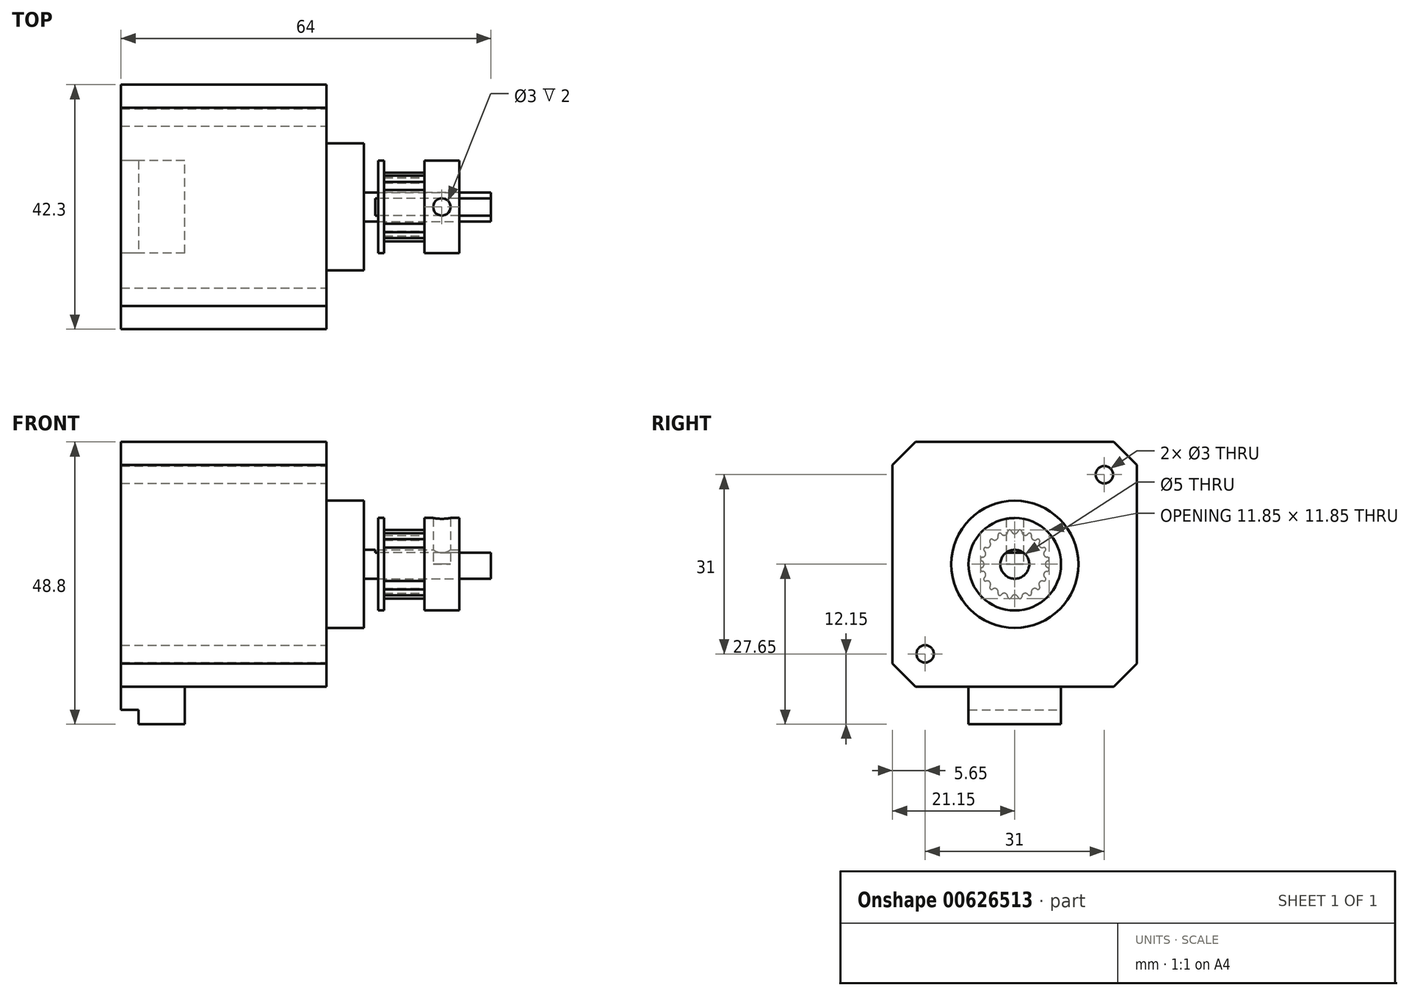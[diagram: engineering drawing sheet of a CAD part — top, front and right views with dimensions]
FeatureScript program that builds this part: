
annotation { "Feature Type Name" : "Feature", "Feature Type Description" : "" }
export const myFeature = defineFeature(function(context is Context, id is Id, definition is map)
    precondition{}
    {
        {
            var Q0;
            Q0=qCreatedBy(makeId("Right.planeOp"),FACE);
            var sketch = newSketch(context, id + "F0", { "sketchPlane" : qUnion([Q0]), "asVersion" : FeatureScriptVersionNumber.V275_SKETCH_PATTERN_LOWER_LIMIT});
            skLineSegment(sketch, "E0", {"start": v(0, 0) * mm, "end": v(-19.15, 19.15) * mm, "construction": true});
            skLineSegment(sketch, "E1", {"start": v(-19.15, 19.15) * mm, "end": v(-17.15, 21.15) * mm});
            skLineSegment(sketch, "E2", {"start": v(-17.15, 21.15) * mm, "end": v(0, 21.15) * mm});
            skCircle(sketch, "E3", {"center": v(-15.5, 15.5) * mm, "radius": 1.5 * mm});
            skLineSegment(sketch, "E4.MirrorCS", {"start": v(-19.15, 19.15) * mm, "end": v(-21.15, 17.15) * mm});
            skLineSegment(sketch, "E5.MirrorCS", {"start": v(-21.15, 17.15) * mm, "end": v(-21.15, 0) * mm});
            skLineSegment(sketch, "E6.MirrorCS", {"start": v(17.15, 21.15) * mm, "end": v(0, 21.15) * mm});
            skCircle(sketch, "E7.MirrorC", {"center": v(15.5, 15.5) * mm, "radius": 1.5 * mm});
            skLineSegment(sketch, "E8.MirrorCS", {"start": v(19.15, 19.15) * mm, "end": v(17.15, 21.15) * mm});
            skLineSegment(sketch, "E9.MirrorCS", {"start": v(19.15, 19.15) * mm, "end": v(21.15, 17.15) * mm});
            skLineSegment(sketch, "E10.MirrorCS", {"start": v(21.15, 17.15) * mm, "end": v(21.15, 0) * mm});
            skLineSegment(sketch, "E11.MirrorCS", {"start": v(-21.15, -17.15) * mm, "end": v(-21.15, 0) * mm});
            skLineSegment(sketch, "E12.MirrorCS", {"start": v(-19.15, -19.15) * mm, "end": v(-21.15, -17.15) * mm});
            skLineSegment(sketch, "E13.MirrorCS", {"start": v(-19.15, -19.15) * mm, "end": v(-17.15, -21.15) * mm});
            skCircle(sketch, "E14.MirrorC", {"center": v(-15.5, -15.5) * mm, "radius": 1.5 * mm});
            skLineSegment(sketch, "E15.MirrorCS", {"start": v(-17.15, -21.15) * mm, "end": v(0, -21.15) * mm});
            skLineSegment(sketch, "E16.MirrorCS", {"start": v(17.15, -21.15) * mm, "end": v(0, -21.15) * mm});
            skLineSegment(sketch, "E17.MirrorCS", {"start": v(19.15, -19.15) * mm, "end": v(17.15, -21.15) * mm});
            skCircle(sketch, "E18.MirrorC", {"center": v(15.5, -15.5) * mm, "radius": 1.5 * mm});
            skLineSegment(sketch, "E19.MirrorCS", {"start": v(19.15, -19.15) * mm, "end": v(21.15, -17.15) * mm});
            skLineSegment(sketch, "E20.MirrorCS", {"start": v(21.15, -17.15) * mm, "end": v(21.15, 0) * mm});
            skCircle(sketch, "E21", {"center": v(0, 0) * mm, "radius": 11 * mm});
            skCircle(sketch, "E22", {"center": v(0, 0) * mm, "radius": 2.5 * mm});
            skLineSegment(sketch, "E23", {"start": v(-1.5, 2) * mm, "end": v(1.5, 2) * mm});
            skSolve(sketch);
        }
        {
            var Q0;
            {var subQ0=sQuery(id+"F0.wireOp",EDGE,"E23");Q0=makeQuery(id+"F0.imprint","IMPRINT",FACE,{"disambiguationData":[TD([[makeQuery(id+"F0.imprint","IMPRINT",EDGE,{"derivedFrom":subQ0}),1.0]])]});}
            var Q1;
            {var subQ0=sQuery(id+"F0.wireOp",EDGE,"E23");Q1=makeQuery(id+"F0.imprint","IMPRINT",FACE,{"disambiguationData":[TD([[makeQuery(id+"F0.imprint","IMPRINT",EDGE,{"derivedFrom":subQ0}),-1.0]])]});}
            var Q2;
            Q2=makeQuery(id+"F0.imprint","IMPRINT",FACE,{"disambiguationData":[TD([[makeQuery(id+"F0.imprint","IMPRINT",EDGE,{"derivedFrom":sQuery(id+"F0.wireOp",EDGE,"E21")}),1.0]])]});
            var Q3;
            Q3=makeQuery(id+"F0.imprint","IMPRINT",FACE,{"disambiguationData":[TD([[makeQuery(id+"F0.imprint","IMPRINT",EDGE,{"derivedFrom":sQuery(id+"F0.wireOp",EDGE,"E7.MirrorC")}),-1.0]])]});
            var Q4;
            Q4=makeQuery(id+"F0.imprint","IMPRINT",FACE,{"disambiguationData":[TD([[makeQuery(id+"F0.imprint","IMPRINT",EDGE,{"derivedFrom":sQuery(id+"F0.wireOp",EDGE,"E18.MirrorC")}),1.0]])]});
            var Q5;
            Q5=makeQuery(id+"F0.imprint","IMPRINT",FACE,{"disambiguationData":[TD([[makeQuery(id+"F0.imprint","IMPRINT",EDGE,{"derivedFrom":sQuery(id+"F0.wireOp",EDGE,"E14.MirrorC")}),-1.0]])]});
            var Q6;
            Q6=makeQuery(id+"F0.imprint","IMPRINT",FACE,{"disambiguationData":[TD([[makeQuery(id+"F0.imprint","IMPRINT",EDGE,{"derivedFrom":sQuery(id+"F0.wireOp",EDGE,"E3")}),1.0]])]});
            var Q7;
            Q7=makeQuery(id+"F0.imprint","IMPRINT",FACE,{"disambiguationData":[TD([[makeQuery(id+"F0.imprint","IMPRINT",EDGE,{"derivedFrom":sQuery(id+"F0.wireOp",EDGE,"E1")}),-1.0]])]});
            extrude(context, id + "F1", {"entities" : qUnion([Q0, Q1, Q2, Q3, Q4, Q5, Q6, Q7]), "oppositeDirection" : true, "depth" : 40 * mm});
        }
        {
            var Q0;
            {var subQ0=sQuery(id+"F0.wireOp",EDGE,"E23");Q0=makeQuery(id+"F0.imprint","IMPRINT",FACE,{"disambiguationData":[TD([[makeQuery(id+"F0.imprint","IMPRINT",EDGE,{"derivedFrom":subQ0}),-1.0]])]});}
            extrude(context, id + "F2", {"entities" : qUnion([Q0]), "operationType" : NewBodyOperationType.ADD, "depth" : 24 * mm});
        }
        {
            var Q0;
            {var subQ0=sQuery(id+"F0.wireOp",EDGE,"E23");Q0=makeQuery(id+"F0.imprint","IMPRINT",FACE,{"disambiguationData":[TD([[makeQuery(id+"F0.imprint","IMPRINT",EDGE,{"derivedFrom":subQ0}),1.0]])]});}
            extrude(context, id + "F3", {"entities" : qUnion([Q0]), "operationType" : NewBodyOperationType.ADD, "depth" : 4 * mm});
        }
        {
            var Q0;
            Q0=makeQuery(id+"F0.imprint","IMPRINT",FACE,{"disambiguationData":[TD([[makeQuery(id+"F0.imprint","IMPRINT",EDGE,{"derivedFrom":sQuery(id+"F0.wireOp",EDGE,"E21")}),1.0]])]});
            extrude(context, id + "F4", {"entities" : qUnion([Q0]), "operationType" : NewBodyOperationType.ADD, "depth" : 2 * mm});
        }
        {
            var Q0;
            Q0=makeQuery(id+"F0.imprint","IMPRINT",FACE,{"disambiguationData":[TD([[makeQuery(id+"F0.imprint","IMPRINT",EDGE,{"derivedFrom":sQuery(id+"F0.wireOp",EDGE,"E3")}),1.0]])]});
            var Q1;
            Q1=makeQuery(id+"F0.imprint","IMPRINT",FACE,{"disambiguationData":[TD([[makeQuery(id+"F0.imprint","IMPRINT",EDGE,{"derivedFrom":sQuery(id+"F0.wireOp",EDGE,"E7.MirrorC")}),-1.0]])]});
            var Q2;
            Q2=makeQuery(id+"F0.imprint","IMPRINT",FACE,{"disambiguationData":[TD([[makeQuery(id+"F0.imprint","IMPRINT",EDGE,{"derivedFrom":sQuery(id+"F0.wireOp",EDGE,"E18.MirrorC")}),1.0]])]});
            var Q3;
            Q3=makeQuery(id+"F0.imprint","IMPRINT",FACE,{"disambiguationData":[TD([[makeQuery(id+"F0.imprint","IMPRINT",EDGE,{"derivedFrom":sQuery(id+"F0.wireOp",EDGE,"E14.MirrorC")}),-1.0]])]});
            extrude(context, id + "F5", {"entities" : qUnion([Q0, Q1, Q2, Q3]), "operationType" : NewBodyOperationType.REMOVE, "oppositeDirection" : true, "depth" : 4.5 * mm});
        }
        {
            var Q0;
            Q0=makeQuery(id+"F1.opExtrude","CAP_FACE",FACE,{"disambiguationData":[OSD([sQuery(id+"F0.wireOp",EDGE,"E1"),sQuery(id+"F0.wireOp",EDGE,"E2"),sQuery(id+"F0.wireOp",EDGE,"E4.MirrorCS"),sQuery(id+"F0.wireOp",EDGE,"E5.MirrorCS"),sQuery(id+"F0.wireOp",EDGE,"E6.MirrorCS"),sQuery(id+"F0.wireOp",EDGE,"E8.MirrorCS"),sQuery(id+"F0.wireOp",EDGE,"E9.MirrorCS"),sQuery(id+"F0.wireOp",EDGE,"E10.MirrorCS"),sQuery(id+"F0.wireOp",EDGE,"E11.MirrorCS"),sQuery(id+"F0.wireOp",EDGE,"E12.MirrorCS"),sQuery(id+"F0.wireOp",EDGE,"E13.MirrorCS"),sQuery(id+"F0.wireOp",EDGE,"E15.MirrorCS"),sQuery(id+"F0.wireOp",EDGE,"E16.MirrorCS"),sQuery(id+"F0.wireOp",EDGE,"E17.MirrorCS"),sQuery(id+"F0.wireOp",EDGE,"E19.MirrorCS"),sQuery(id+"F0.wireOp",EDGE,"E20.MirrorCS")])],"isStart":false});
            var sketch = newSketch(context, id + "F6", { "sketchPlane" : qUnion([Q0]), "asVersion" : FeatureScriptVersionNumber.V275_SKETCH_PATTERN_LOWER_LIMIT});
            skLineSegment(sketch, "E24", {"start": v(-8, -21.15) * mm, "end": v(-8, -27.65) * mm});
            skLineSegment(sketch, "E25.MirrorCS", {"start": v(8, -21.15) * mm, "end": v(8, -27.65) * mm});
            skLineSegment(sketch, "E26", {"start": v(-8, -27.65) * mm, "end": v(8, -27.65) * mm});
            skLineSegment(sketch, "E27", {"start": v(-8, -21.15) * mm, "end": v(8, -21.15) * mm});
            skLineSegment(sketch, "E28", {"start": v(8, -25.15) * mm, "end": v(-8, -25.15) * mm});
            skSolve(sketch);
        }
        {
            var Q0;
            {var subQ0=sQuery(id+"F6.wireOp",EDGE,"E27");Q0=makeQuery(id+"F6.imprint","IMPRINT",FACE,{"disambiguationData":[TD([[makeQuery(id+"F6.imprint","IMPRINT",EDGE,{"derivedFrom":subQ0}),1.0]])]});}
            var Q1;
            {var subQ1=sQuery(id+"F6.wireOp",EDGE,"E26");Q1=makeQuery(id+"F6.imprint","IMPRINT",FACE,{"disambiguationData":[TD([[makeQuery(id+"F6.imprint","IMPRINT",EDGE,{"derivedFrom":subQ1}),1.0]])]});}
            extrude(context, id + "F7", {"entities" : qUnion([Q0, Q1]), "operationType" : NewBodyOperationType.ADD, "oppositeDirection" : true, "depth" : 11 * mm});
        }
        {
            var Q0;
            {var subQ1=sQuery(id+"F6.wireOp",EDGE,"E26");Q0=makeQuery(id+"F6.imprint","IMPRINT",FACE,{"disambiguationData":[TD([[makeQuery(id+"F6.imprint","IMPRINT",EDGE,{"derivedFrom":subQ1}),1.0]])]});}
            extrude(context, id + "F8", {"entities" : qUnion([Q0]), "operationType" : NewBodyOperationType.REMOVE, "oppositeDirection" : true, "depth" : 3 * mm});
        }
        {
            var Q0;
            Q0=qCreatedBy(makeId("Right.planeOp"),FACE);
            cPlane(context, id + "F9", {"entities" : qUnion([Q0]), "cplaneType" : CPlaneType.OFFSET, "offset" : 9 * mm, "width" : 150 * mm, "height" : 150 * mm});
        }
        {
            var Q0;
            Q0=qCreatedBy(id+"F9.planeOp",FACE);
            var sketch = newSketch(context, id + "F10", { "sketchPlane" : qUnion([Q0]), "asVersion" : FeatureScriptVersionNumber.V275_SKETCH_PATTERN_LOWER_LIMIT});
            skCircle(sketch, "E29", {"center": v(0, 0) * mm, "radius": 8 * mm});
            skCircle(sketch, "E30", {"center": v(0, 0) * mm, "radius": 2.5 * mm});
            skSolve(sketch);
        }
        {
            var Q0;
            Q0=makeQuery(id+"F10.imprint","IMPRINT",FACE,{"disambiguationData":[TD([[makeQuery(id+"F10.imprint","IMPRINT",EDGE,{"derivedFrom":sQuery(id+"F10.wireOp",EDGE,"E29")}),1.0]])]});
            extrude(context, id + "F11", {"entities" : qUnion([Q0]), "oppositeDirection" : true, "depth" : 4.5 * mm, "hasSecondDirection" : true, "secondDirectionOppositeDirection" : false, "secondDirectionDepth" : 9.5 * mm});
        }
        {
            var Q0;
            Q0=qCreatedBy(id+"F9.planeOp",FACE);
            var sketch = newSketch(context, id + "F12", { "sketchPlane" : qUnion([Q0]), "asVersion" : FeatureScriptVersionNumber.V275_SKETCH_PATTERN_LOWER_LIMIT});
            skArc(sketch, "E31", {"start": v(-0.57, 5.7) * mm, "mid": v(0, 5.3) * mm, "end": v(0.57, 5.7) * mm});
            skArc(sketch, "E32", {"start": v(0.94, 5.93) * mm, "mid": v(0.71, 5.88) * mm, "end": v(0.57, 5.7) * mm});
            skLineSegment(sketch, "E33", {"start": v(0, 5.9) * mm, "end": v(0, 0) * mm, "construction": true});
            skLineSegment(sketch, "E34", {"start": v(0, 0) * mm, "end": v(0.94, 5.93) * mm, "construction": true});
            skArc(sketch, "E35.MirrorCS", {"start": v(-0.94, 5.93) * mm, "mid": v(-0.71, 5.88) * mm, "end": v(-0.57, 5.7) * mm});
            skArc(sketch, "E36.1.0", {"start": v(2.72, 5.35) * mm, "mid": v(2.5, 5.37) * mm, "end": v(2.3, 5.25) * mm});
            skArc(sketch, "E36.1.1", {"start": v(1.22, 5.6) * mm, "mid": v(1.64, 5.04) * mm, "end": v(2.3, 5.25) * mm});
            skArc(sketch, "E36.1.2", {"start": v(0.94, 5.93) * mm, "mid": v(1.14, 5.81) * mm, "end": v(1.22, 5.6) * mm});
            skArc(sketch, "E36.2.0", {"start": v(4.24, 4.24) * mm, "mid": v(4.03, 4.34) * mm, "end": v(3.81, 4.28) * mm});
            skArc(sketch, "E36.2.1", {"start": v(2.9, 4.95) * mm, "mid": v(3.12, 4.29) * mm, "end": v(3.81, 4.28) * mm});
            skArc(sketch, "E36.2.2", {"start": v(2.72, 5.35) * mm, "mid": v(2.88, 5.18) * mm, "end": v(2.9, 4.95) * mm});
            skArc(sketch, "E36.3.0", {"start": v(5.35, 2.72) * mm, "mid": v(5.18, 2.88) * mm, "end": v(4.95, 2.9) * mm});
            skArc(sketch, "E36.3.1", {"start": v(4.28, 3.81) * mm, "mid": v(4.29, 3.12) * mm, "end": v(4.95, 2.9) * mm});
            skArc(sketch, "E36.3.2", {"start": v(4.24, 4.24) * mm, "mid": v(4.34, 4.03) * mm, "end": v(4.28, 3.81) * mm});
            skArc(sketch, "E36.4.0", {"start": v(5.93, 0.94) * mm, "mid": v(5.81, 1.14) * mm, "end": v(5.6, 1.22) * mm});
            skArc(sketch, "E36.4.1", {"start": v(5.25, 2.3) * mm, "mid": v(5.04, 1.64) * mm, "end": v(5.6, 1.22) * mm});
            skArc(sketch, "E36.4.2", {"start": v(5.35, 2.72) * mm, "mid": v(5.37, 2.5) * mm, "end": v(5.25, 2.3) * mm});
            skArc(sketch, "E36.5.0", {"start": v(5.93, -0.94) * mm, "mid": v(5.88, -0.71) * mm, "end": v(5.7, -0.57) * mm});
            skArc(sketch, "E36.5.1", {"start": v(5.7, 0.57) * mm, "mid": v(5.3, 0) * mm, "end": v(5.7, -0.57) * mm});
            skArc(sketch, "E36.5.2", {"start": v(5.93, 0.94) * mm, "mid": v(5.88, 0.71) * mm, "end": v(5.7, 0.57) * mm});
            skArc(sketch, "E36.6.0", {"start": v(5.35, -2.72) * mm, "mid": v(5.37, -2.5) * mm, "end": v(5.25, -2.3) * mm});
            skArc(sketch, "E36.6.1", {"start": v(5.6, -1.22) * mm, "mid": v(5.04, -1.64) * mm, "end": v(5.25, -2.3) * mm});
            skArc(sketch, "E36.6.2", {"start": v(5.93, -0.94) * mm, "mid": v(5.81, -1.14) * mm, "end": v(5.6, -1.22) * mm});
            skArc(sketch, "E36.7.0", {"start": v(4.24, -4.24) * mm, "mid": v(4.34, -4.03) * mm, "end": v(4.28, -3.81) * mm});
            skArc(sketch, "E36.7.1", {"start": v(4.95, -2.9) * mm, "mid": v(4.29, -3.12) * mm, "end": v(4.28, -3.81) * mm});
            skArc(sketch, "E36.7.2", {"start": v(5.35, -2.72) * mm, "mid": v(5.18, -2.88) * mm, "end": v(4.95, -2.9) * mm});
            skArc(sketch, "E36.8.0", {"start": v(2.72, -5.35) * mm, "mid": v(2.88, -5.18) * mm, "end": v(2.9, -4.95) * mm});
            skArc(sketch, "E36.8.1", {"start": v(3.81, -4.28) * mm, "mid": v(3.12, -4.29) * mm, "end": v(2.9, -4.95) * mm});
            skArc(sketch, "E36.8.2", {"start": v(4.24, -4.24) * mm, "mid": v(4.03, -4.34) * mm, "end": v(3.81, -4.28) * mm});
            skArc(sketch, "E36.9.0", {"start": v(0.94, -5.93) * mm, "mid": v(1.14, -5.81) * mm, "end": v(1.22, -5.6) * mm});
            skArc(sketch, "E36.9.1", {"start": v(2.3, -5.25) * mm, "mid": v(1.64, -5.04) * mm, "end": v(1.22, -5.6) * mm});
            skArc(sketch, "E36.9.2", {"start": v(2.72, -5.35) * mm, "mid": v(2.5, -5.37) * mm, "end": v(2.3, -5.25) * mm});
            skArc(sketch, "E36.10.0", {"start": v(-0.94, -5.93) * mm, "mid": v(-0.71, -5.88) * mm, "end": v(-0.57, -5.7) * mm});
            skArc(sketch, "E36.10.1", {"start": v(0.57, -5.7) * mm, "mid": v(0, -5.3) * mm, "end": v(-0.57, -5.7) * mm});
            skArc(sketch, "E36.10.2", {"start": v(0.94, -5.93) * mm, "mid": v(0.71, -5.88) * mm, "end": v(0.57, -5.7) * mm});
            skArc(sketch, "E36.11.0", {"start": v(-2.72, -5.35) * mm, "mid": v(-2.5, -5.37) * mm, "end": v(-2.3, -5.25) * mm});
            skArc(sketch, "E36.11.1", {"start": v(-1.22, -5.6) * mm, "mid": v(-1.64, -5.04) * mm, "end": v(-2.3, -5.25) * mm});
            skArc(sketch, "E36.11.2", {"start": v(-0.94, -5.93) * mm, "mid": v(-1.14, -5.81) * mm, "end": v(-1.22, -5.6) * mm});
            skArc(sketch, "E36.12.0", {"start": v(-4.24, -4.24) * mm, "mid": v(-4.03, -4.34) * mm, "end": v(-3.81, -4.28) * mm});
            skArc(sketch, "E36.12.1", {"start": v(-2.9, -4.95) * mm, "mid": v(-3.12, -4.29) * mm, "end": v(-3.81, -4.28) * mm});
            skArc(sketch, "E36.12.2", {"start": v(-2.72, -5.35) * mm, "mid": v(-2.88, -5.18) * mm, "end": v(-2.9, -4.95) * mm});
            skArc(sketch, "E36.13.0", {"start": v(-5.35, -2.72) * mm, "mid": v(-5.18, -2.88) * mm, "end": v(-4.95, -2.9) * mm});
            skArc(sketch, "E36.13.1", {"start": v(-4.28, -3.81) * mm, "mid": v(-4.29, -3.12) * mm, "end": v(-4.95, -2.9) * mm});
            skArc(sketch, "E36.13.2", {"start": v(-4.24, -4.24) * mm, "mid": v(-4.34, -4.03) * mm, "end": v(-4.28, -3.81) * mm});
            skArc(sketch, "E36.14.0", {"start": v(-5.93, -0.94) * mm, "mid": v(-5.81, -1.14) * mm, "end": v(-5.6, -1.22) * mm});
            skArc(sketch, "E36.14.1", {"start": v(-5.25, -2.3) * mm, "mid": v(-5.04, -1.64) * mm, "end": v(-5.6, -1.22) * mm});
            skArc(sketch, "E36.14.2", {"start": v(-5.35, -2.72) * mm, "mid": v(-5.37, -2.5) * mm, "end": v(-5.25, -2.3) * mm});
            skArc(sketch, "E36.15.0", {"start": v(-5.93, 0.94) * mm, "mid": v(-5.88, 0.71) * mm, "end": v(-5.7, 0.57) * mm});
            skArc(sketch, "E36.15.1", {"start": v(-5.7, -0.57) * mm, "mid": v(-5.3, 0) * mm, "end": v(-5.7, 0.57) * mm});
            skArc(sketch, "E36.15.2", {"start": v(-5.93, -0.94) * mm, "mid": v(-5.88, -0.71) * mm, "end": v(-5.7, -0.57) * mm});
            skArc(sketch, "E36.16.0", {"start": v(-5.35, 2.72) * mm, "mid": v(-5.37, 2.5) * mm, "end": v(-5.25, 2.3) * mm});
            skArc(sketch, "E36.16.1", {"start": v(-5.6, 1.22) * mm, "mid": v(-5.04, 1.64) * mm, "end": v(-5.25, 2.3) * mm});
            skArc(sketch, "E36.16.2", {"start": v(-5.93, 0.94) * mm, "mid": v(-5.81, 1.14) * mm, "end": v(-5.6, 1.22) * mm});
            skArc(sketch, "E36.17.0", {"start": v(-4.24, 4.24) * mm, "mid": v(-4.34, 4.03) * mm, "end": v(-4.28, 3.81) * mm});
            skArc(sketch, "E36.17.1", {"start": v(-4.95, 2.9) * mm, "mid": v(-4.29, 3.12) * mm, "end": v(-4.28, 3.81) * mm});
            skArc(sketch, "E36.17.2", {"start": v(-5.35, 2.72) * mm, "mid": v(-5.18, 2.88) * mm, "end": v(-4.95, 2.9) * mm});
            skArc(sketch, "E36.18.0", {"start": v(-2.72, 5.35) * mm, "mid": v(-2.88, 5.18) * mm, "end": v(-2.9, 4.95) * mm});
            skArc(sketch, "E36.18.1", {"start": v(-3.81, 4.28) * mm, "mid": v(-3.12, 4.29) * mm, "end": v(-2.9, 4.95) * mm});
            skArc(sketch, "E36.18.2", {"start": v(-4.24, 4.24) * mm, "mid": v(-4.03, 4.34) * mm, "end": v(-3.81, 4.28) * mm});
            skArc(sketch, "E36.19.0", {"start": v(-0.94, 5.93) * mm, "mid": v(-1.14, 5.81) * mm, "end": v(-1.22, 5.6) * mm});
            skArc(sketch, "E36.19.1", {"start": v(-2.3, 5.25) * mm, "mid": v(-1.64, 5.04) * mm, "end": v(-1.22, 5.6) * mm});
            skArc(sketch, "E36.19.2", {"start": v(-2.72, 5.35) * mm, "mid": v(-2.5, 5.37) * mm, "end": v(-2.3, 5.25) * mm});
            skPoint(sketch, "E36.center", {"position": v(0, 0) * mm});
            skLineSegment(sketch, "E36.anchor1", {"start": v(0, 0) * mm, "end": v(0.57, 5.7) * mm, "construction": true});
            skLineSegment(sketch, "E36.anchor2", {"start": v(0, 0) * mm, "end": v(-1.22, 5.6) * mm, "construction": true});
            skCircle(sketch, "E37", {"center": v(0, 0) * mm, "radius": 8 * mm});
            skSolve(sketch);
        }
        {
            var Q0;
            Q0=makeQuery(id+"F12.imprint","IMPRINT",FACE,{"disambiguationData":[TD([[makeQuery(id+"F12.imprint","IMPRINT",EDGE,{"derivedFrom":sQuery(id+"F12.wireOp",EDGE,"E31")}),1.0]])]});
            extrude(context, id + "F13", {"entities" : qUnion([Q0]), "operationType" : NewBodyOperationType.REMOVE, "oppositeDirection" : true, "depth" : 7 * mm, "symmetric" : true});
        }
        {
            var Q0;
            Q0=qCreatedBy(makeId("Top.planeOp"),FACE);
            var sketch = newSketch(context, id + "F14", { "sketchPlane" : qUnion([Q0]), "asVersion" : FeatureScriptVersionNumber.V275_SKETCH_PATTERN_LOWER_LIMIT});
            skCircle(sketch, "E38", {"center": v(15.5, 0) * mm, "radius": 1.5 * mm});
            skSolve(sketch);
        }
        {
            var Q0;
            Q0=makeQuery(id+"F14.imprint","IMPRINT",FACE,{"disambiguationData":[TD([[makeQuery(id+"F14.imprint","IMPRINT",EDGE,{"derivedFrom":sQuery(id+"F14.wireOp",EDGE,"E38")}),1.0]])]});
            extrude(context, id + "F15", {"entities" : qUnion([Q0]), "operationType" : NewBodyOperationType.REMOVE, "depth" : 25 * mm});
        }
    });
